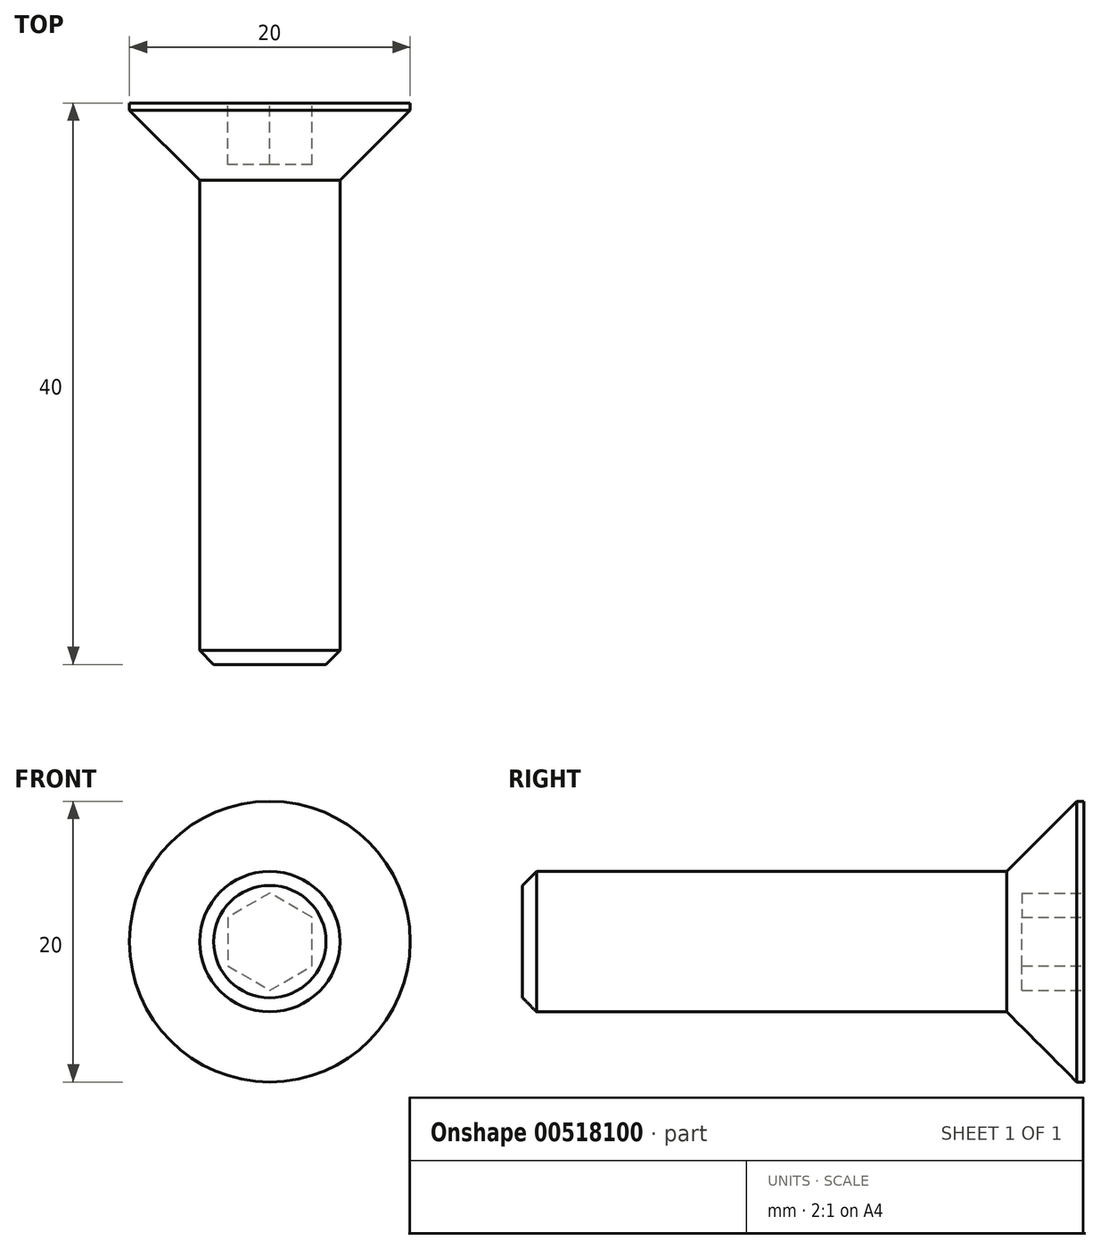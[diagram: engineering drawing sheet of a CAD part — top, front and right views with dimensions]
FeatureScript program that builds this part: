
annotation { "Feature Type Name" : "Feature", "Feature Type Description" : "" }
export const myFeature = defineFeature(function(context is Context, id is Id, definition is map)
    precondition{}
    {
        {
            assignVariable(context, id + "F0", {"name" : "t", "anyValue" : 4.4});
        }
        {
            var Q0;
            Q0=qCreatedBy(makeId("Right.planeOp"),FACE);
            var sketch = newSketch(context, id + "F1", { "sketchPlane" : qUnion([Q0])});
            skLineSegment(sketch, "E0", {"start": v(0, 0) * mm, "end": v(0, 10) * mm});
            skLineSegment(sketch, "E1", {"start": v(0, 10) * mm, "end": v(-0.5, 10) * mm});
            skLineSegment(sketch, "E2", {"start": v(-0.5, 10) * mm, "end": v(-5.5, 5) * mm});
            skLineSegment(sketch, "E3", {"start": v(-5.5, 5) * mm, "end": v(-39, 5) * mm});
            skLineSegment(sketch, "E4", {"start": v(-39, 5) * mm, "end": v(-40, 4) * mm});
            skLineSegment(sketch, "E5", {"start": v(-40, 4) * mm, "end": v(-40, 0) * mm});
            skLineSegment(sketch, "E6", {"start": v(-40, 0) * mm, "end": v(0, 0) * mm});
            skSolve(sketch);
        }
        {
            var Q0;
            Q0=makeQuery(id+"F1.imprint","IMPRINT",FACE,{"disambiguationData":[TD([[makeQuery(id+"F1.imprint","IMPRINT",EDGE,{"derivedFrom":sQuery(id+"F1.wireOp",EDGE,"E0")}),1.0]])]});
            var Q1;
            Q1=sQuery(id+"F1.wireOp",EDGE,"E6");
            revolve(context, id + "F2", {"entities" : qUnion([Q0]), "axis" : qUnion([Q1]), "revolveType" : RevolveType.FULL});
        }
        {
            var Q0;
            Q0=makeQuery(id+"F2.opRevolve","SWEPT_FACE",FACE,{"disambiguationData":[OSD([sQuery(id+"F1.wireOp",EDGE,"E0")])]});
            var sketch = newSketch(context, id + "F3", { "sketchPlane" : qUnion([Q0])});
            skCircle(sketch, "E7.cCircle", {"center": v(0, 0) * mm, "radius": 3.46 * mm, "construction": true});
            skLineSegment(sketch, "E7.0", {"start": v(0, 3.46) * mm, "end": v(3, 1.73) * mm});
            skLineSegment(sketch, "E7.1", {"start": v(3, 1.73) * mm, "end": v(3, -1.73) * mm});
            skLineSegment(sketch, "E7.2", {"start": v(3, -1.73) * mm, "end": v(0, -3.46) * mm});
            skLineSegment(sketch, "E7.3", {"start": v(0, -3.46) * mm, "end": v(-3, -1.73) * mm});
            skLineSegment(sketch, "E7.4", {"start": v(-3, -1.73) * mm, "end": v(-3, 1.73) * mm});
            skLineSegment(sketch, "E7.5", {"start": v(-3, 1.73) * mm, "end": v(0, 3.46) * mm});
            skSolve(sketch);
        }
        {
            var Q0;
            Q0=qSketchRegion(id+"F3",true);
            extrude(context, id + "F4", {"entities" : qUnion([Q0]), "operationType" : NewBodyOperationType.REMOVE, "oppositeDirection" : true, "depth" : (getVariable(context, 't')) * mm, "offsetDistance" : 25 * mm});
        }
    });
